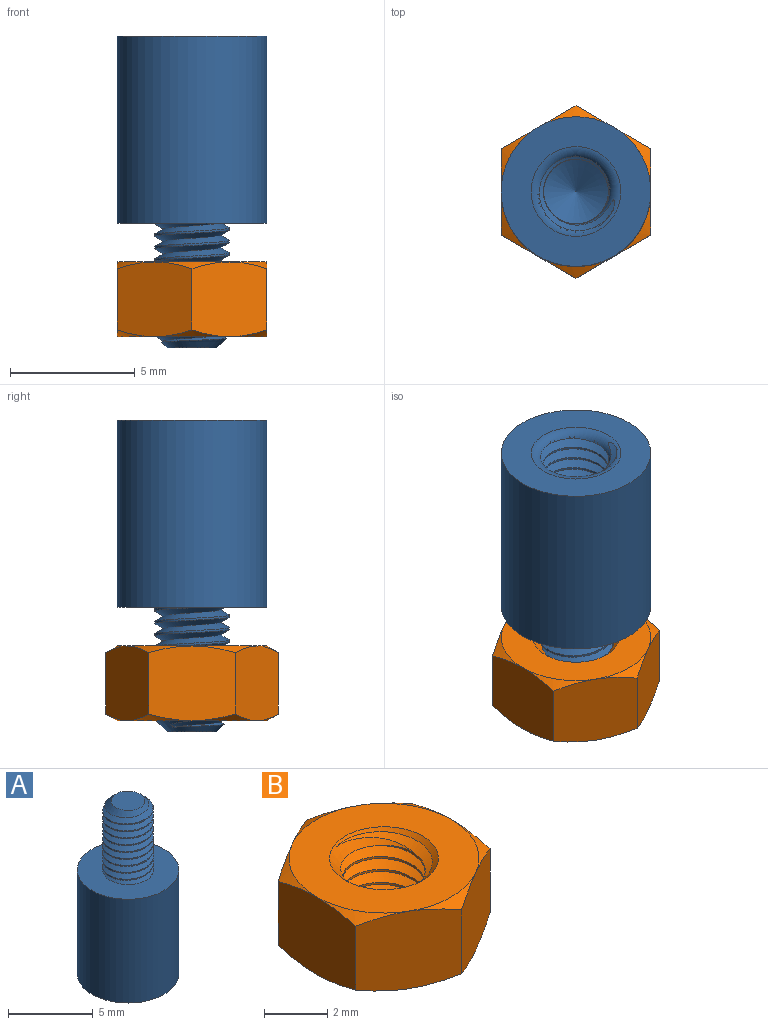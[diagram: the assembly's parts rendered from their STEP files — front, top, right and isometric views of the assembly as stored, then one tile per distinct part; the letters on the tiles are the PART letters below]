
ASSEMBLY  parts=2 mates=1
PART A: 18 faces, bbox 6x6x12.8 mm
  f0: cylinder r=1.5mm len=4.5mm, axis (0,0,-1), area 7.1mm2, adj f2,f8,f12,f13
  f1: cylinder r=3mm len=7.5mm, axis (0,0,-1), area 141.4mm2, adj f2,f3
  f2: plane 6x6mm, normal (0,0,1), area 21.2mm2, adj f0,f1,f11
  f3: plane 6x6mm, normal (0,0,-1), area 18.1mm2, adj f1,f14
  f4: plane 2x2mm, normal (0,0,1), area 3.1mm2, adj f7
  f5: cone r=0mm half-angle=59deg, axis (0,0,-1), area 6.2mm2, adj f6
  f6: cylinder r=1.3mm len=3.5mm, axis (0,0,-1), area 6.7mm2, adj f5,f14,f15,f16,f17
  f7: cone r=1mm half-angle=45deg, axis (0,0,-1), area 3.6mm2, adj f4,f8,f9,f12
  f8: cone r=1mm half-angle=45deg, axis (0,0,-1), area 0.2mm2, adj f0,f7,f13
  f9: plane 0.17x0.13mm, normal (0,-1,0), area 0mm2, adj f7,f12,f13
  f10: plane 0.42x0.36mm, normal (0,1,0), area 0.1mm2, adj f11,f12,f13
  f11: cylinder r=1.5mm len=3mm, axis (0,0,-1), area 1.7mm2, adj f2,f10,f13
  f12: bspline ~5.21x3.46mm, area 33.2mm2, adj f0,f7,f9,f10,f13
  f13: bspline ~5.21x3.46mm, area 34.8mm2, adj f0,f8,f9,f10,f11,f12
  f14: torus R=1.8mm, axis (0,0,1), area 4.3mm2, adj f3,f6,f16,f17
  f15: plane 0.42x0.36mm, normal (0,-1,0), area 0.1mm2, adj f6,f16,f17
  f16: bspline ~4.04x3.84mm, area 29.5mm2, adj f6,f14,f15,f17
  f17: bspline ~4.04x3.84mm, area 27.6mm2, adj f6,f14,f15,f16
PART B: 24 faces, bbox 7.2x7.2x3.7 mm
  f0: plane 6x6mm, normal (0,0,1), area 19mm2, adj f5,f6,f8,f10,f12,f14,f21
  f1: plane 6.26x6.26mm, normal (0,0,-1), area 21.6mm2, adj f2,f3,f4,f7,f9,f11,f13,f22
  f2: cylinder r=1.3mm len=2.6mm, axis (0,0,-1), area 3.4mm2, adj f1,f21,f22,f23
  f3: cone r=5.44mm half-angle=60deg, axis (0,0,1), area 0.9mm2, adj f1,f15,f20
  f4: cone r=5.44mm half-angle=60deg, axis (0,0,1), area 0.9mm2, adj f1,f15,f16
  f5: cone r=5.44mm half-angle=60deg, axis (0,0,-1), area 0.9mm2, adj f0,f15,f20
  f6: cone r=5.44mm half-angle=60deg, axis (0,0,-1), area 0.9mm2, adj f0,f15,f16
  f7: cone r=5.44mm half-angle=60deg, axis (0,0,1), area 0.9mm2, adj f1,f16,f17
  f8: cone r=5.44mm half-angle=60deg, axis (0,0,-1), area 0.9mm2, adj f0,f16,f17
  f9: cone r=5.44mm half-angle=60deg, axis (0,0,1), area 0.9mm2, adj f1,f17,f18
  f10: cone r=5.44mm half-angle=60deg, axis (0,0,-1), area 0.9mm2, adj f0,f17,f18
  f11: cone r=5.44mm half-angle=60deg, axis (0,0,1), area 0.9mm2, adj f1,f18,f19
  f12: cone r=5.44mm half-angle=60deg, axis (0,0,-1), area 0.9mm2, adj f0,f18,f19
  f13: cone r=5.44mm half-angle=60deg, axis (0,0,1), area 0.9mm2, adj f1,f19,f20
  f14: cone r=5.44mm half-angle=60deg, axis (0,0,-1), area 0.9mm2, adj f0,f19,f20
  f15: plane 3.75x3.29mm, normal (-1,0,0), area 9.8mm2, adj f3,f4,f5,f6,f16,f20
  f16: plane 3.29x3.28mm, normal (-0.5,0.87,0), area 9.8mm2, adj f4,f6,f7,f8,f15,f17
  f17: plane 3.29x3.28mm, normal (0.5,0.87,0), area 9.8mm2, adj f7,f8,f9,f10,f16,f18
  f18: plane 3.75x3.29mm, normal (1,0,0), area 9.8mm2, adj f9,f10,f11,f12,f17,f19
  f19: plane 3.29x3.28mm, normal (0.5,-0.87,0), area 9.8mm2, adj f11,f12,f13,f14,f18,f20
  f20: plane 3.29x3.28mm, normal (-0.5,-0.87,0), area 9.8mm2, adj f3,f5,f13,f14,f15,f19
  f21: cone r=1.3mm half-angle=45deg, axis (0,0,1), area 3.7mm2, adj f0,f2,f22,f23
  f22: bspline ~3.84x3.38mm, area 21.7mm2, adj f1,f2,f21,f23
  f23: bspline ~3.84x3.33mm, area 21.7mm2, adj f1,f2,f21,f22
PLACE A rot(axis=(-0.35,-0.94,0),180deg) t=(-1.35,0.77,10.44)mm
PLACE B t=(-1.35,0.77,-1.62)mm fixed
MATE cylindrical A.f0 <-> B.f3  axis (0,0,1) through (-1.35,0.77,-1.81)mm
